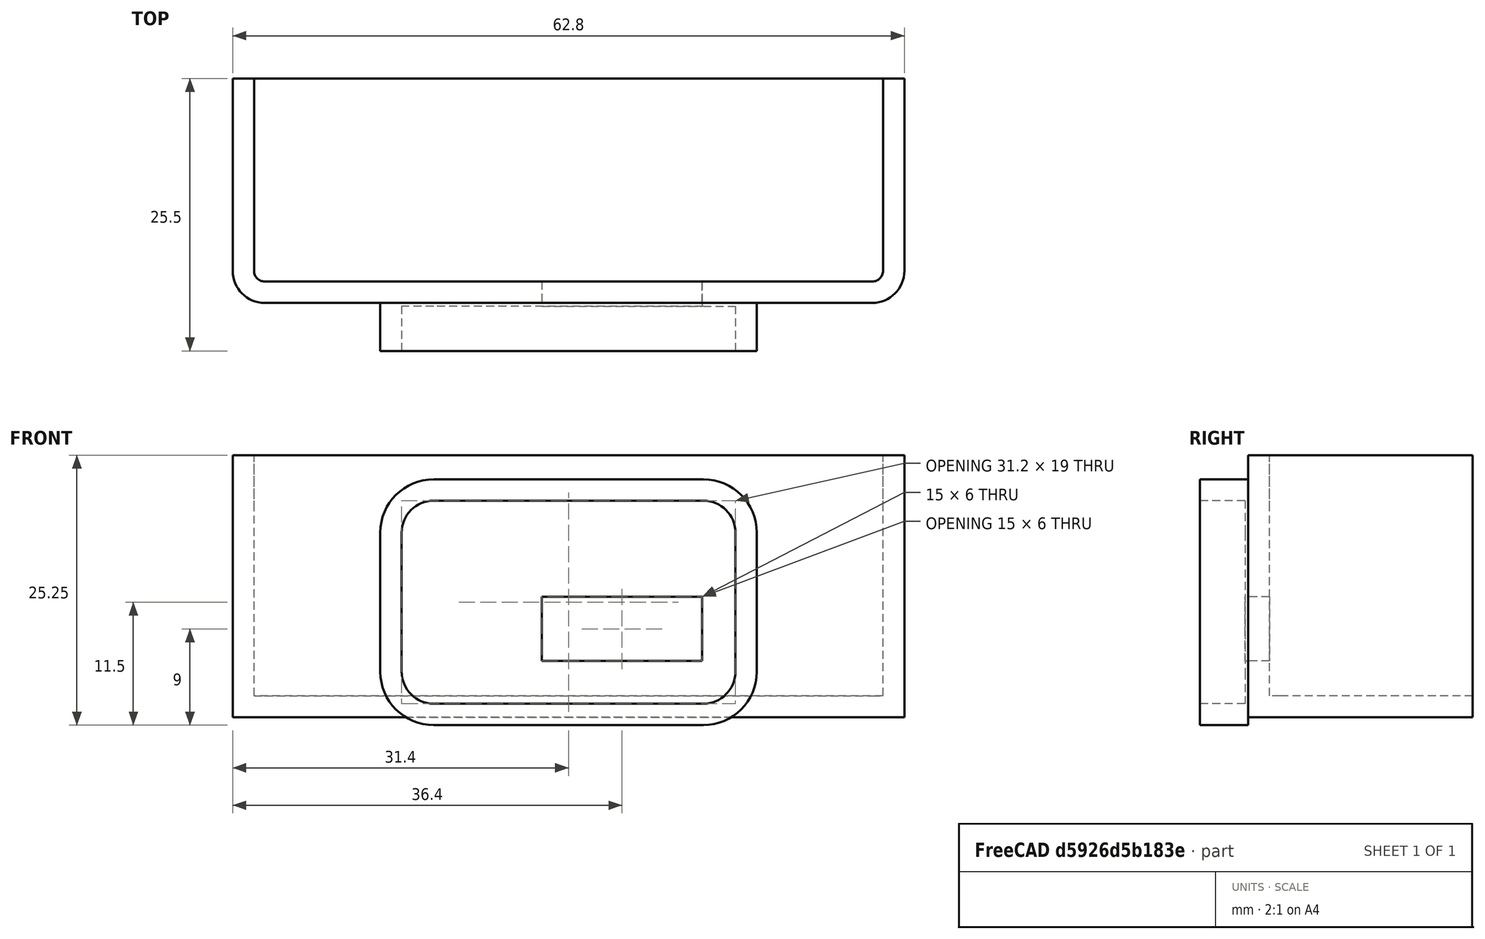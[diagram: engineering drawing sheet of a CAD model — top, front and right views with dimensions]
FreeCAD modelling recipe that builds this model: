
FCSTD DOCUMENT  (FreeCAD 0.20R28671 (Git))
Label: enganche boquilla
License: All rights reserved
LicenseURL: http://en.wikipedia.org/wiki/All_rights_reserved
objects: TechDraw::DrawViewDimension×16, Sketcher::SketchObject×6, PartDesign::Pad×5, TechDraw::DrawViewAnnotation×3, PartDesign::Pocket×2, TechDraw::DrawProjGroupItem×2, PartDesign::Fillet×1, PartDesign::Body×1, TechDraw::DrawSVGTemplate×1, Part::Refine×1, TechDraw::DrawProjGroup×1, TechDraw::DrawViewSection×1, TechDraw::DrawViewSymbol×1, TechDraw::DrawPage×1
note: 24 computed .brp shape members not serialized (recipe doc carries the construction recipe); baked Part::Feature solids carry a one-line shape summary decoded from their .brp

FEATURE [Sketcher::SketchObject] Sketch
  FullyConstrained = true
  MapMode = 5
  Support = -> [XY_Plane]
  sketch-geometry (6):
    g0: LineSegment StartX=-31.4 StartY=0 StartZ=0 EndX=31.4 EndY=0 EndZ=0
    g1: LineSegment StartX=31.4 StartY=0 StartZ=0 EndX=31.4 EndY=21 EndZ=0
    g2: LineSegment StartX=31.4 StartY=21 StartZ=0 EndX=-31.4 EndY=21 EndZ=0
    g3: LineSegment StartX=-31.4 StartY=21 StartZ=0 EndX=-31.4 EndY=0 EndZ=0
    g4: LineSegment StartX=-31.4 StartY=0 StartZ=0 EndX=0 EndY=0 EndZ=0
    g5: LineSegment StartX=0 StartY=0 StartZ=0 EndX=31.4 EndY=0 EndZ=0
  constraints (16):
    c: Coincident(g0,g1)
    c: Coincident(g1,g2)
    c: Coincident(g2,g3)
    c: Coincident(g3,g0)
    c: Horizontal(g0)
    c: Horizontal(g2)
    c: Vertical(g1)
    c: Vertical(g3)
    c: PointOnObject(g0,g-1)
    c: Coincident(g4,g0)
    c: Coincident(g5,g4)
    c: Coincident(g5,g0)
    c: Equal(g5,g4)
    c: Coincident(g4,g-1)
    c: DistanceX(g0,g0) = 62.8
    c: DistanceY(g3,g3) = 21
FEATURE [PartDesign::Pad] Pad
  Direction = (0,0,1)
  Length = 2
  Length2 = 100
  Profile = -> Sketch
  ReferenceAxis = -> Sketch [N_Axis]
  Type = 0
FEATURE [PartDesign::Fillet] Fillet
  Base = -> Pad [Edge1,Edge2]
  BaseFeature = -> Pad
  Radius = 3
  SupportTransform = false
  UseAllEdges = false
FEATURE [Sketcher::SketchObject] Sketch001
  ExternalGeometry = -> [Fillet]
  FullyConstrained = true
  MapMode = 5
  Placement = pos=(0,0,2) rot=(0,0,1;0rad)
  Support = -> [Fillet]
  sketch-geometry (13):
    g0: LineSegment StartX=-31.4 StartY=21 StartZ=0 EndX=-31.4 EndY=3 EndZ=0
    g1: LineSegment StartX=31.4 StartY=21 StartZ=0 EndX=31.4 EndY=3 EndZ=0
    g2: LineSegment StartX=-28.4 StartY=0 StartZ=0 EndX=28.4 EndY=-4e-16 EndZ=0
    g3: ArcOfCircle CenterX=-28.4 CenterY=3 CenterZ=0 NormalX=0 NormalY=0 NormalZ=1 AngleXU=0 Radius=3 StartAngle=3.14159 EndAngle=4.71239
    g4: ArcOfCircle CenterX=28.4 CenterY=3 CenterZ=0 NormalX=0 NormalY=0 NormalZ=1 AngleXU=0 Radius=3 StartAngle=4.71239 EndAngle=6.28319
    g5: LineSegment StartX=-31.4 StartY=21 StartZ=0 EndX=-29.4 EndY=21 EndZ=0
    g6: LineSegment StartX=-29.4 StartY=21 StartZ=0 EndX=-29.4 EndY=3 EndZ=0
    g7: LineSegment StartX=31.4 StartY=21 StartZ=0 EndX=29.4 EndY=21 EndZ=0
    g8: LineSegment StartX=29.4 StartY=21 StartZ=0 EndX=29.4 EndY=3 EndZ=0
    g9: LineSegment StartX=-28.4 StartY=2 StartZ=0 EndX=28.4 EndY=2 EndZ=0
    g10: ArcOfCircle CenterX=-28.4 CenterY=3 CenterZ=0 NormalX=0 NormalY=0 NormalZ=1 AngleXU=0 Radius=1 StartAngle=3.14159 EndAngle=4.71239
    g11: ArcOfCircle CenterX=28.4 CenterY=3 CenterZ=0 NormalX=0 NormalY=0 NormalZ=1 AngleXU=0 Radius=1 StartAngle=4.71239 EndAngle=6.28319
    g12: LineSegment StartX=-28.4 StartY=2 StartZ=0 EndX=-28.4 EndY=0 EndZ=0
  constraints (30):
    c: Coincident(g0,g-3)
    c: Coincident(g0,g-4)
    c: Coincident(g1,g-7)
    c: Coincident(g1,g-7)
    c: Coincident(g2,g-5)
    c: Coincident(g2,g-6)
    c: Coincident(g3,g0)
    c: Coincident(g4,g1)
    c: Coincident(g5,g0)
    c: Horizontal(g5)
    c: Coincident(g6,g5)
    c: Vertical(g6)
    c: Coincident(g7,g1)
    c: Horizontal(g7)
    c: Coincident(g8,g7)
    c: Vertical(g8)
    c: Horizontal(g9)
    c: Tangent(g11,g9) = -1.5708
    c: Tangent(g11,g8) = 1.5708
    c: Equal(g10,g11)
    c: Equal(g5,g7)
    c: Tangent(g10,g9) = -1.5708
    c: DistanceX(g5,g5) = 2
    c: Tangent(g10,g6) = -1.5708
    c: Coincident(g12,g9)
    c: PointOnObject(g12,g2)
    c: Vertical(g12)
    c: Coincident(g10,g3)
    c: Tangent(g3,g2) = -1.5708
    c: Tangent(g4,g2) = -1.5708
FEATURE [PartDesign::Pad] Pad001
  BaseFeature = -> Fillet
  Direction = (0,0,1)
  Length = 17.5
  Length2 = 100
  Profile = -> Sketch001
  ReferenceAxis = -> Sketch001 [N_Axis]
  Type = 0
FEATURE [Sketcher::SketchObject] Sketch002
  ExternalGeometry = -> [Pad001]
  FullyConstrained = true
  MapMode = 5
  Placement = pos=(0,-3e-16,0) rot=(1,0,0;1.5708rad)
  Support = -> [Pad001]
  sketch-geometry (9):
    g0: LineSegment StartX=-14 StartY=18.75 StartZ=0 EndX=14 EndY=18.75 EndZ=0
    g1: LineSegment StartX=14 StartY=18.75 StartZ=0 EndX=14 EndY=2.75 EndZ=0
    g2: LineSegment StartX=14 StartY=2.75 StartZ=0 EndX=-14 EndY=2.75 EndZ=0
    g3: LineSegment StartX=-14 StartY=2.75 StartZ=0 EndX=-14 EndY=18.75 EndZ=0
    g4: LineSegment StartX=-14 StartY=18.75 StartZ=0 EndX=0 EndY=10.75 EndZ=0
    g5: LineSegment StartX=0 StartY=10.75 StartZ=0 EndX=14 EndY=2.75 EndZ=0
    g6: LineSegment StartX=28.4 StartY=19.5 StartZ=0 EndX=28.4 EndY=10.75 EndZ=0
    g7: LineSegment StartX=28.4 StartY=10.75 StartZ=0 EndX=28.4 EndY=2 EndZ=0
    g8: Circle CenterX=10 CenterY=7.75 CenterZ=0 NormalX=0 NormalY=0 NormalZ=1 AngleXU=0 Radius=2.5
  constraints (25):
    c: Coincident(g0,g1)
    c: Coincident(g1,g2)
    c: Coincident(g2,g3)
    c: Coincident(g3,g0)
    c: Horizontal(g0)
    c: Horizontal(g2)
    c: Vertical(g1)
    c: Vertical(g3)
    c: DistanceX(g2,g2) = 28
    c: DistanceY(g1,g1) = 16
    c: Coincident(g4,g0)
    c: Coincident(g5,g4)
    c: Coincident(g5,g1)
    c: Equal(g5,g4)
    c: Parallel(g5,g4)
    c: Vertical(g4,g-1)
    c: Coincident(g6,g-3)
    c: Coincident(g7,g6)
    c: Coincident(g7,g-3)
    c: Equal(g6,g7)
    c: Horizontal(g6,g4)
    c: Vertical(g6)
    c: DistanceX(g8,g1) = 4
    c: DistanceY(g1,g8) = 5
    c: Diameter(g8) = 5
FEATURE [PartDesign::Pocket] Pocket
  BaseFeature = -> Pad001
  Direction = (0,1,-2e-16)
  Length = 5
  Length2 = 100
  Profile = -> Sketch002
  Type = 2
FEATURE [Sketcher::SketchObject] Sketch003
  ExternalGeometry = -> [Pocket]
  FullyConstrained = true
  MapMode = 5
  Placement = pos=(0,-3e-16,0) rot=(1,0,0;1.5708rad)
  Support = -> [Pocket]
  sketch-geometry (26):
    g0: LineSegment StartX=-28.4 StartY=19.5 StartZ=0 EndX=0 EndY=10.75 EndZ=0
    g1: LineSegment StartX=2e-16 StartY=10.75 StartZ=0 EndX=28.4 EndY=2 EndZ=0
    g2: ArcOfCircle CenterX=-12.6 CenterY=17.25 CenterZ=0 NormalX=0 NormalY=0 NormalZ=1 AngleXU=0 Radius=3 StartAngle=1.5708 EndAngle=3.14159
    g3: LineSegment StartX=-12.6 StartY=20.25 StartZ=0 EndX=12.6 EndY=20.25 EndZ=0
    g4: ArcOfCircle CenterX=12.6 CenterY=17.25 CenterZ=0 NormalX=0 NormalY=0 NormalZ=1 AngleXU=0 Radius=3 StartAngle=1e-16 EndAngle=1.5708
    g5: LineSegment StartX=15.6 StartY=17.25 StartZ=0 EndX=15.6 EndY=4.25 EndZ=0
    g6: ArcOfCircle CenterX=12.6 CenterY=4.25 CenterZ=0 NormalX=0 NormalY=0 NormalZ=1 AngleXU=0 Radius=3 StartAngle=4.71239 EndAngle=6.28319
    g7: LineSegment StartX=12.6 StartY=1.25 StartZ=0 EndX=-12.6 EndY=1.25 EndZ=0
    g8: ArcOfCircle CenterX=-12.6 CenterY=4.25 CenterZ=0 NormalX=0 NormalY=0 NormalZ=1 AngleXU=0 Radius=3 StartAngle=3.14159 EndAngle=4.71239
    g9: LineSegment StartX=-15.6 StartY=4.25 StartZ=0 EndX=-15.6 EndY=17.25 EndZ=0
    g10: GeomPoint X=-15.6 Y=20.25 Z=0
    g11: GeomPoint X=15.6 Y=1.25 Z=0
    g12: LineSegment StartX=-12.6 StartY=17.25 StartZ=0 EndX=0 EndY=10.75 EndZ=0
    g13: LineSegment StartX=2e-16 StartY=10.75 StartZ=0 EndX=12.6 EndY=4.25 EndZ=0
    g14: ArcOfCircle CenterX=-12.6 CenterY=17.25 CenterZ=0 NormalX=0 NormalY=0 NormalZ=1 AngleXU=0 Radius=5 StartAngle=1.5708 EndAngle=3.14159
    g15: LineSegment StartX=-12.6 StartY=22.25 StartZ=0 EndX=12.6 EndY=22.25 EndZ=0
    g16: ArcOfCircle CenterX=12.6 CenterY=17.25 CenterZ=0 NormalX=0 NormalY=0 NormalZ=1 AngleXU=0 Radius=5 StartAngle=1e-16 EndAngle=1.5708
    g17: LineSegment StartX=17.6 StartY=17.25 StartZ=0 EndX=17.6 EndY=4.25 EndZ=0
    g18: ArcOfCircle CenterX=12.6 CenterY=4.25 CenterZ=0 NormalX=0 NormalY=0 NormalZ=1 AngleXU=0 Radius=5 StartAngle=4.71239 EndAngle=6.28319
    g19: LineSegment StartX=12.6 StartY=-0.75 StartZ=0 EndX=-12.6 EndY=-0.75 EndZ=0
    g20: ArcOfCircle CenterX=-12.6 CenterY=4.25 CenterZ=0 NormalX=0 NormalY=0 NormalZ=1 AngleXU=0 Radius=5 StartAngle=3.14159 EndAngle=4.71239
    g21: LineSegment StartX=-17.6 StartY=4.25 StartZ=0 EndX=-17.6 EndY=17.25 EndZ=0
    g22: GeomPoint X=-17.6 Y=22.25 Z=0
    g23: GeomPoint X=17.6 Y=-0.75 Z=0
    g24: LineSegment StartX=-12.6 StartY=-0.75 StartZ=0 EndX=0 EndY=10.75 EndZ=0
    g25: LineSegment StartX=2e-16 StartY=10.75 StartZ=0 EndX=12.6 EndY=22.25 EndZ=0
  constraints (60):
    c: Coincident(g0,g-4)
    c: Coincident(g1,g0)
    c: Coincident(g1,g-3)
    c: Equal(g1,g0)
    c: Parallel(g1,g0)
    c: Tangent(g2,g3) = 1.5708
    c: Tangent(g3,g4) = 1.5708
    c: Tangent(g4,g5) = 1.5708
    c: Tangent(g5,g6) = 1.5708
    c: Tangent(g6,g7) = 1.5708
    c: Tangent(g7,g8) = 1.5708
    c: Tangent(g8,g9) = 1.5708
    c: Tangent(g9,g2) = 1.5708
    c: Horizontal(g3)
    c: Horizontal(g7)
    c: Vertical(g5)
    c: Vertical(g9)
    c: Equal(g2,g4)
    c: Equal(g4,g6)
    c: Equal(g6,g8)
    c: PointOnObject(g10,g3)
    c: PointOnObject(g10,g9)
    c: PointOnObject(g11,g5)
    c: PointOnObject(g11,g7)
    c: Radius(g4) = 3
    c: DistanceX(g8,g5) = 31.2
    c: DistanceY(g7,g2) = 19
    c: Coincident(g12,g2)
    c: Coincident(g12,g0)
    c: Coincident(g13,g0)
    c: Coincident(g13,g6)
    c: Parallel(g13,g12)
    c: Equal(g13,g12)
    c: Tangent(g14,g15) = 1.5708
    c: Tangent(g15,g16) = 1.5708
    c: Tangent(g16,g17) = 1.5708
    c: Tangent(g17,g18) = 1.5708
    c: Tangent(g18,g19) = 1.5708
    c: Tangent(g19,g20) = 1.5708
    c: Tangent(g20,g21) = 1.5708
    c: Tangent(g21,g14) = 1.5708
    c: Horizontal(g15)
    c: Horizontal(g19)
    c: Vertical(g17)
    c: Vertical(g21)
    c: Equal(g14,g16)
    c: Equal(g16,g18)
    c: Equal(g18,g20)
    c: PointOnObject(g22,g15)
    c: PointOnObject(g22,g21)
    c: PointOnObject(g23,g17)
    c: PointOnObject(g23,g19)
    c: Coincident(g20,g8)
    c: Coincident(g24,g19)
    c: Coincident(g25,g24)
    c: Coincident(g25,g15)
    c: Parallel(g25,g24)
    c: Equal(g24,g25)
    c: Coincident(g24,g0)
    c: DistanceY(g19,g7) = 2
FEATURE [PartDesign::Pad] Pad002
  BaseFeature = -> Pocket
  Direction = (0,-1,2e-16)
  Length = 4.5
  Length2 = 100
  Profile = -> Sketch003
  ReferenceAxis = -> Sketch003 [N_Axis]
  Type = 0
FEATURE [Sketcher::SketchObject] Sketch004
  ExternalGeometry = -> [Pad002]
  FullyConstrained = true
  MapMode = 5
  Placement = pos=(0,-3e-16,0) rot=(1,0,0;1.5708rad)
  Support = -> [Pad002]
  sketch-geometry (9):
    g0: Circle CenterX=10 CenterY=7.75 CenterZ=0 NormalX=0 NormalY=0 NormalZ=1 AngleXU=0 Radius=2.5
    g1: LineSegment StartX=-12.6 StartY=20.25 StartZ=0 EndX=12.6 EndY=20.25 EndZ=0
    g2: LineSegment StartX=12.6 StartY=1.25 StartZ=0 EndX=-12.6 EndY=1.25 EndZ=0
    g3: LineSegment StartX=-15.6 StartY=17.25 StartZ=0 EndX=-15.6 EndY=4.25 EndZ=0
    g4: LineSegment StartX=15.6 StartY=17.25 StartZ=0 EndX=15.6 EndY=4.25 EndZ=0
    g5: ArcOfCircle CenterX=-12.6 CenterY=17.25 CenterZ=0 NormalX=0 NormalY=0 NormalZ=1 AngleXU=0 Radius=3 StartAngle=1.5708 EndAngle=3.14159
    g6: ArcOfCircle CenterX=12.6 CenterY=17.25 CenterZ=0 NormalX=0 NormalY=0 NormalZ=1 AngleXU=0 Radius=3 StartAngle=4e-16 EndAngle=1.5708
    g7: ArcOfCircle CenterX=12.6 CenterY=4.25 CenterZ=0 NormalX=0 NormalY=0 NormalZ=1 AngleXU=0 Radius=3 StartAngle=4.71239 EndAngle=6.28319
    g8: ArcOfCircle CenterX=-12.6 CenterY=4.25 CenterZ=0 NormalX=0 NormalY=0 NormalZ=1 AngleXU=0 Radius=3 StartAngle=3.14159 EndAngle=4.71239
  constraints (18):
    c: Diameter(g0) = 5
    c: Coincident(g5,g3)
    c: Coincident(g6,g1)
    c: Coincident(g7,g2)
    c: Coincident(g8,g3)
    c: Tangent(g7,g4) = 1.5708
    c: Tangent(g6,g4) = 1.5708
    c: Coincident(g1,g-3)
    c: Coincident(g-3,g1)
    c: Coincident(g4,g-4)
    c: Coincident(g4,g-4)
    c: Coincident(g-6,g2)
    c: Coincident(g2,g-6)
    c: Coincident(g3,g-7)
    c: Coincident(g3,g-7)
    c: Coincident(g-5,g0)
    c: Tangent(g5,g1) = 1.5708
    c: Tangent(g8,g2) = 1.5708
FEATURE [PartDesign::Pad] Pad003
  BaseFeature = -> Pad002
  Direction = (0,-1,2e-16)
  Length = 0.3
  Length2 = 100
  Profile = -> Sketch004
  ReferenceAxis = -> Sketch004 [N_Axis]
  Type = 0
FEATURE [PartDesign::Pad] Pad004
  BaseFeature = -> Pad003
  Direction = (0,0,1)
  Length = 5
  Length2 = 100
  Profile = -> Pad003 [Face16]
  Type = 0
FEATURE [Sketcher::SketchObject] Sketch005
  ExternalGeometry = -> [Pad004]
  FullyConstrained = true
  MapMode = 5
  Placement = pos=(0,2,0) rot=(0,0.707107,0.707107;3.14159rad)
  Support = -> [Pad004]
  sketch-geometry (4):
    g0: LineSegment StartX=-12.5 StartY=11.25 StartZ=0 EndX=2.5 EndY=11.25 EndZ=0
    g1: LineSegment StartX=2.5 StartY=11.25 StartZ=0 EndX=2.5 EndY=5.25 EndZ=0
    g2: LineSegment StartX=2.5 StartY=5.25 StartZ=0 EndX=-12.5 EndY=5.25 EndZ=0
    g3: LineSegment StartX=-12.5 StartY=5.25 StartZ=0 EndX=-12.5 EndY=11.25 EndZ=0
  constraints (12):
    c: Coincident(g0,g1)
    c: Coincident(g1,g2)
    c: Coincident(g2,g3)
    c: Coincident(g3,g0)
    c: Horizontal(g0)
    c: Horizontal(g2)
    c: Vertical(g1)
    c: Vertical(g3)
    c: Tangent(g2,g-3)
    c: Tangent(g-3,g3)
    c: DistanceY(g3,g3) = 6
    c: DistanceX(g0,g0) = 15
FEATURE [PartDesign::Pocket] Pocket001
  BaseFeature = -> Pad004
  Direction = (0,-1,2e-16)
  Length = 5
  Length2 = 100
  Profile = -> Sketch005
  Type = 0
FEATURE [PartDesign::Body] Body
  Group = -> [Sketch,Pad,Fillet,Sketch001,Pad001,Sketch002,Pocket,Sketch003,Pad002,Sketch004,Pad003,Pad004,Sketch005,Pocket001]
  Origin = -> Origin
  Tip = -> Pocket001
FEATURE [TechDraw::DrawSVGTemplate] Template003
  EditableTexts = AUTHOR_NAME=Daniel García García; DATE=13-04-2022; DN=5; DOCUMENT_TYPE=Plano de pieza; PN=6; REVISION=1; SCALE=1:1; SHEET=5/15; SIZE=A4; TITLELINE-1=Enganche de la Boquilla
  Height = 210
  Orientation = 1
  Width = 297
FEATURE [Part::Refine] Pocket001001
  Source = -> Pocket001
FEATURE [TechDraw::DrawProjGroupItem] ProjItem  label="Front"
  CoarseView = false
  Direction = (0,-1,0)
  Focus = 100
  HardHidden = false
  IsoCount = 0
  IsoHidden = false
  IsoVisible = false
  LockPosition = true
  Perspective = false
  Rotation = 0
  RotationVector = (1,0,0)
  ScaleType = 2
  SeamHidden = false
  SeamVisible = true
  SmoothHidden = false
  SmoothVisible = true
  Source = -> [Pocket001001]
  Type = 0
  X = 0
  XDirection = (1,0,0)
  Y = 0
FEATURE [TechDraw::DrawProjGroupItem] ProjItem001  label="Top"
  CoarseView = false
  Direction = (0,0,1)
  Focus = 100
  HardHidden = false
  IsoCount = 0
  IsoHidden = false
  IsoVisible = false
  LockPosition = true
  Perspective = false
  Rotation = 0
  RotationVector = (1,0,0)
  ScaleType = 2
  SeamHidden = false
  SeamVisible = true
  SmoothHidden = false
  SmoothVisible = true
  Source = -> [Pocket001001]
  Type = 4
  X = 0
  XDirection = (1,0,0)
  Y = -58.3571
FEATURE [TechDraw::DrawProjGroup] ProjGroup
  Anchor = -> ProjItem
  AutoDistribute = true
  LockPosition = false
  ProjectionType = 0
  Rotation = 0
  ScaleType = 0
  Source = -> [Pocket001001]
  Views = -> [ProjItem,ProjItem001]
  X = 206.614
  Y = 144.775
  spacingX = 15
  spacingY = 15
FEATURE [TechDraw::DrawViewSection] SectionView  label="Section A - A"
  BaseView = -> ProjItem
  CoarseView = false
  CutSurfaceDisplay = 2
  Direction = (1,0,0)
  FileGeomPattern = <path>
  FileHatchPattern = <path>
  Focus = 100
  FuseBeforeCut = false
  HardHidden = false
  HatchScale = 1
  IsoCount = 0
  IsoHidden = false
  IsoVisible = false
  LockPosition = true
  NameGeomPattern = Diamond
  Perspective = false
  Rotation = 0
  ScaleType = 2
  SeamHidden = false
  SeamVisible = true
  SectionDirection = 1
  SectionNormal = (1,0,0)
  SectionOrigin = (0,8.25,11.88)
  SectionSymbol = A
  SmoothHidden = false
  SmoothVisible = true
  Source = -> [Pocket001001]
  X = 81.5716
  XDirection = (0,1,0)
  Y = 144.78
FEATURE [TechDraw::DrawViewDimension] Dimension
  AngleOverride = false
  Arbitrary = false
  ArbitraryTolerances = false
  EqualTolerance = true
  ExtensionAngle = 0
  FormatSpec = %.2w
  FormatSpecOverTolerance = %+.2w
  FormatSpecUnderTolerance = %+.2w
  Inverted = false
  LineAngle = 0
  LockPosition = false
  MeasureType = 1
  OverTolerance = 0
  References2D = -> [SectionView]
  Rotation = 0
  ScaleType = 0
  TheoreticalExact = false
  Type = 2
  UnderTolerance = 0
  X = 24.7058
  Y = -4.93567
FEATURE [TechDraw::DrawViewDimension] Dimension001
  AngleOverride = false
  Arbitrary = false
  ArbitraryTolerances = false
  EqualTolerance = true
  ExtensionAngle = 0
  FormatSpec = %.2w
  FormatSpecOverTolerance = %+.2w
  FormatSpecUnderTolerance = %+.2w
  Inverted = false
  LineAngle = 0
  LockPosition = false
  MeasureType = 1
  OverTolerance = 0
  References2D = -> [SectionView]
  Rotation = 0
  ScaleType = 0
  TheoreticalExact = false
  Type = 1
  UnderTolerance = 0
  X = -7.57756
  Y = 26.917
FEATURE [TechDraw::DrawViewDimension] Dimension002
  AngleOverride = false
  Arbitrary = false
  ArbitraryTolerances = false
  EqualTolerance = true
  ExtensionAngle = 0
  FormatSpec = %.2w
  FormatSpecOverTolerance = %+.2w
  FormatSpecUnderTolerance = %+.2w
  Inverted = false
  LineAngle = 0
  LockPosition = false
  MeasureType = 1
  OverTolerance = 0
  References2D = -> [ProjItem001]
  Rotation = 0
  ScaleType = 0
  TheoreticalExact = false
  Type = 2
  UnderTolerance = 0
  X = -40.234
  Y = 4.53471
FEATURE [TechDraw::DrawViewDimension] Dimension003
  AngleOverride = false
  Arbitrary = false
  ArbitraryTolerances = false
  EqualTolerance = true
  ExtensionAngle = 0
  FormatSpec = %.2w
  FormatSpecOverTolerance = %+.2w
  FormatSpecUnderTolerance = %+.2w
  Inverted = false
  LineAngle = 0
  LockPosition = false
  MeasureType = 1
  OverTolerance = 0
  References2D = -> [ProjItem001]
  Rotation = 0
  ScaleType = 0
  TheoreticalExact = false
  Type = 1
  UnderTolerance = 0
  X = -0.861166
  Y = 20.2017
FEATURE [TechDraw::DrawViewDimension] Dimension004
  AngleOverride = false
  Arbitrary = false
  ArbitraryTolerances = false
  EqualTolerance = true
  ExtensionAngle = 0
  FormatSpec = %.2w
  FormatSpecOverTolerance = %+.2w
  FormatSpecUnderTolerance = %+.2w
  Inverted = false
  LineAngle = 0
  LockPosition = false
  MeasureType = 1
  OverTolerance = 0
  References2D = -> [ProjItem]
  Rotation = 0
  ScaleType = 0
  TheoreticalExact = false
  Type = 1
  UnderTolerance = 0
  X = 0.645875
  Y = 39.4529
FEATURE [TechDraw::DrawViewDimension] Dimension005
  AngleOverride = false
  Arbitrary = false
  ArbitraryTolerances = false
  EqualTolerance = true
  ExtensionAngle = 0
  FormatSpec = R%.2w
  FormatSpecOverTolerance = %+.2w
  FormatSpecUnderTolerance = %+.2w
  Inverted = false
  LineAngle = 0
  LockPosition = false
  MeasureType = 1
  OverTolerance = 0
  References2D = -> [ProjItem001]
  Rotation = 0
  ScaleType = 0
  TheoreticalExact = false
  Type = 4
  UnderTolerance = 0
  X = -42.9836
  Y = -12.459
FEATURE [TechDraw::DrawViewDimension] Dimension006
  AngleOverride = false
  Arbitrary = false
  ArbitraryTolerances = false
  EqualTolerance = true
  ExtensionAngle = 0
  FormatSpec = %.2w
  FormatSpecOverTolerance = %+.2w
  FormatSpecUnderTolerance = %+.2w
  Inverted = false
  LineAngle = 0
  LockPosition = false
  MeasureType = 1
  OverTolerance = 0
  References2D = -> [ProjItem001]
  Rotation = 0
  ScaleType = 0
  TheoreticalExact = false
  Type = 1
  UnderTolerance = 0
  X = 0.411124
  Y = -13.7488
FEATURE [TechDraw::DrawViewDimension] Dimension007
  AngleOverride = false
  Arbitrary = false
  ArbitraryTolerances = false
  EqualTolerance = true
  ExtensionAngle = 0
  FormatSpec = R%.2w
  FormatSpecOverTolerance = %+.2w
  FormatSpecUnderTolerance = %+.2w
  Inverted = false
  LineAngle = 0
  LockPosition = false
  MeasureType = 1
  OverTolerance = 0
  References2D = -> [ProjItem]
  Rotation = 0
  ScaleType = 0
  TheoreticalExact = false
  Type = 4
  UnderTolerance = 0
  X = -36.9483
  Y = 22.4048
FEATURE [TechDraw::DrawViewDimension] Dimension008
  AngleOverride = false
  Arbitrary = false
  ArbitraryTolerances = false
  EqualTolerance = true
  ExtensionAngle = 0
  FormatSpec = %.2w
  FormatSpecOverTolerance = %+.2w
  FormatSpecUnderTolerance = %+.2w
  Inverted = false
  LineAngle = 0
  LockPosition = false
  MeasureType = 1
  OverTolerance = 0
  References2D = -> [ProjItem]
  Rotation = 0
  ScaleType = 0
  TheoreticalExact = false
  Type = 1
  UnderTolerance = 0
  X = 5.39307
  Y = 6.98487
FEATURE [TechDraw::DrawViewDimension] Dimension009
  AngleOverride = false
  Arbitrary = false
  ArbitraryTolerances = false
  EqualTolerance = true
  ExtensionAngle = 0
  FormatSpec = %.2w
  FormatSpecOverTolerance = %+.2w
  FormatSpecUnderTolerance = %+.2w
  Inverted = false
  LineAngle = 0
  LockPosition = false
  MeasureType = 1
  OverTolerance = 0
  References2D = -> [ProjItem]
  Rotation = 0
  ScaleType = 0
  TheoreticalExact = false
  Type = 2
  UnderTolerance = 0
  X = -9.77174
  Y = 3.78834
FEATURE [TechDraw::DrawViewDimension] Dimension010
  AngleOverride = false
  Arbitrary = false
  ArbitraryTolerances = false
  EqualTolerance = true
  ExtensionAngle = 0
  FormatSpec = %.2w
  FormatSpecOverTolerance = %+.2w
  FormatSpecUnderTolerance = %+.2w
  Inverted = false
  LineAngle = 0
  LockPosition = false
  MeasureType = 1
  OverTolerance = 0
  References2D = -> [SectionView]
  Rotation = 0
  ScaleType = 0
  TheoreticalExact = false
  Type = 2
  UnderTolerance = 0
  X = -31.2651
  Y = 2.66675
FEATURE [TechDraw::DrawViewDimension] Dimension011
  AngleOverride = false
  Arbitrary = false
  ArbitraryTolerances = false
  EqualTolerance = true
  ExtensionAngle = 0
  FormatSpec = %.2w
  FormatSpecOverTolerance = %+.2w
  FormatSpecUnderTolerance = %+.2w
  Inverted = false
  LineAngle = 0
  LockPosition = false
  MeasureType = 1
  OverTolerance = 0
  References2D = -> [SectionView]
  Rotation = 0
  ScaleType = 0
  TheoreticalExact = false
  Type = 2
  UnderTolerance = 0
  X = -21.7922
  Y = 1.80558
FEATURE [TechDraw::DrawViewDimension] Dimension012
  AngleOverride = false
  Arbitrary = false
  ArbitraryTolerances = false
  EqualTolerance = true
  ExtensionAngle = 0
  FormatSpec = %.2w
  FormatSpecOverTolerance = %+.2w
  FormatSpecUnderTolerance = %+.2w
  Inverted = false
  LineAngle = 0
  LockPosition = false
  MeasureType = 1
  OverTolerance = 0
  References2D = -> [ProjItem001]
  Rotation = 0
  ScaleType = 0
  TheoreticalExact = false
  Type = 2
  UnderTolerance = 0
  X = 39.0614
  Y = -1.39648
FEATURE [TechDraw::DrawViewDimension] Dimension013
  AngleOverride = false
  Arbitrary = false
  ArbitraryTolerances = false
  EqualTolerance = true
  ExtensionAngle = 0
  FormatSpec = R%.2w
  FormatSpecOverTolerance = %+.2w
  FormatSpecUnderTolerance = %+.2w
  Inverted = false
  LineAngle = 0
  LockPosition = false
  MeasureType = 1
  OverTolerance = 0
  References2D = -> [ProjItem]
  Rotation = 0
  ScaleType = 0
  TheoreticalExact = false
  Type = 4
  UnderTolerance = 0
  X = -27.6291
  Y = -15.788
FEATURE [TechDraw::DrawViewDimension] Dimension015
  AngleOverride = false
  Arbitrary = false
  ArbitraryTolerances = false
  EqualTolerance = true
  ExtensionAngle = 0
  FormatSpec = %.2w
  FormatSpecOverTolerance = %+.2w
  FormatSpecUnderTolerance = %+.2w
  Inverted = false
  LineAngle = 0
  LockPosition = false
  MeasureType = 1
  OverTolerance = 0
  References2D = -> [SectionView]
  Rotation = 0
  ScaleType = 0
  TheoreticalExact = false
  Type = 2
  UnderTolerance = 0
  X = -31.5498
  Y = 14.4739
FEATURE [TechDraw::DrawViewDimension] Dimension016
  AngleOverride = false
  Arbitrary = false
  ArbitraryTolerances = false
  EqualTolerance = true
  ExtensionAngle = 0
  FormatSpec = %.2w
  FormatSpecOverTolerance = %+.2w
  FormatSpecUnderTolerance = %+.2w
  Inverted = false
  LineAngle = 0
  LockPosition = false
  MeasureType = 1
  OverTolerance = 0
  References2D = -> [ProjItem]
  Rotation = 0
  ScaleType = 0
  TheoreticalExact = false
  Type = 2
  UnderTolerance = 0
  X = -39.5811
  Y = 2.875
FEATURE [TechDraw::DrawViewAnnotation] Annotation
  Font = osifont
  LineSpace = 80
  LockPosition = false
  MaxWidth = -1
  Rotation = 0
  ScaleType = 0
  Text = Sección A-A'
  TextSize = 5
  TextStyle = 0
  X = 81.5697
  Y = 119.026
FEATURE [TechDraw::DrawViewSymbol] Symbol
  LockPosition = false
  Rotation = 0
  Scale = 0.3
  ScaleType = 2
  Symbol = <blob: 2444 chars omitted>
  X = 217.487
  Y = 36.9001
FEATURE [TechDraw::DrawViewAnnotation] Annotation001
  Font = osifont
  LineSpace = 80
  LockPosition = false
  MaxWidth = -1
  Rotation = 0
  ScaleType = 0
  Text = Default Text
  TextSize = 5
  TextStyle = 0
  X = 148.5
  Y = 105
FEATURE [TechDraw::DrawViewAnnotation] Annotation002
  Font = osifont
  LineSpace = 80
  LockPosition = false
  MaxWidth = -1
  Rotation = 0
  ScaleType = 0
  Text = '
  TextSize = 5
  TextStyle = 0
  X = 208.951
  Y = 113.151
FEATURE [TechDraw::DrawPage] Page003  label="Enganche Boquilla"
  KeepUpdated = true
  NextBalloonIndex = 1
  ProjectionType = 0
  Template = -> Template003
  Views = -> [ProjGroup,SectionView,Dimension,Dimension001,Dimension002,Dimension003,Dimension004,Dimension005,Dimension006,Dimension007,Dimension008,Dimension009,Dimension010,Dimension011,Dimension012,Dimension013,Dimension015,Dimension016,Annotation,Symbol,Annotation002]
note: 2 file-system paths scrubbed to <path> (originals preserved in the JSON sidecar)
